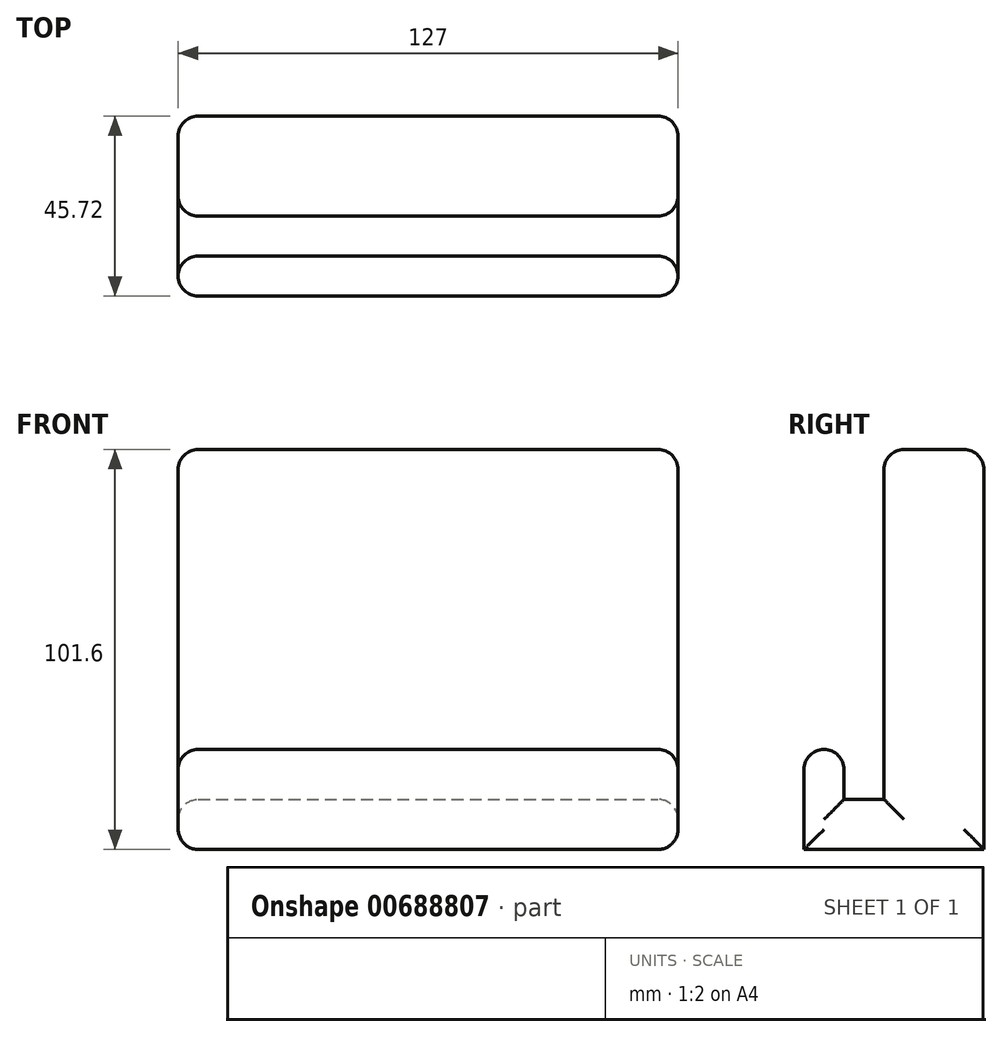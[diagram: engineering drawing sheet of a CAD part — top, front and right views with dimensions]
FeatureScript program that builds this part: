
annotation { "Feature Type Name" : "Feature", "Feature Type Description" : "" }
export const myFeature = defineFeature(function(context is Context, id is Id, definition is map)
    precondition{}
    {
        {
            var Q0;
            Q0=qCreatedBy(makeId("Front.planeOp"),FACE);
            var sketch = newSketch(context, id + "F0", { "sketchPlane" : qUnion([Q0])});
            skLineSegment(sketch, "E0", {"start": v(0, 0) * mm, "end": v(-127, 0) * mm});
            skLineSegment(sketch, "E1", {"start": v(-127, 0) * mm, "end": v(-127, 101.6) * mm});
            skLineSegment(sketch, "E2", {"start": v(0, 0) * mm, "end": v(0, 101.6) * mm});
            skLineSegment(sketch, "E3", {"start": v(0, 101.6) * mm, "end": v(-127, 101.6) * mm});
            skSolve(sketch);
        }
        {
            var Q0;
            Q0=makeQuery(id+"F0.imprint","IMPRINT",FACE,{"disambiguationData":[TD([[makeQuery(id+"F0.imprint","IMPRINT",EDGE,{"derivedFrom":sQuery(id+"F0.wireOp",EDGE,"E0")}),-1.0]])]});
            extrude(context, id + "F1", {"entities" : qUnion([Q0]), "depth" : 25.4 * mm, "offsetDistance" : 25.4 * mm});
        }
        {
            var Q0;
            Q0=makeQuery(id+"F1.opExtrude","CAP_FACE",FACE,{"disambiguationData":[OSD([sQuery(id+"F0.wireOp",EDGE,"E0"),sQuery(id+"F0.wireOp",EDGE,"E1"),sQuery(id+"F0.wireOp",EDGE,"E2"),sQuery(id+"F0.wireOp",EDGE,"E3")])],"isStart":false});
            var sketch = newSketch(context, id + "F2", { "sketchPlane" : qUnion([Q0])});
            skLineSegment(sketch, "E4", {"start": v(-127, 0) * mm, "end": v(-127, 12.7) * mm});
            skLineSegment(sketch, "E5", {"start": v(-127, 12.7) * mm, "end": v(0, 12.7) * mm});
            skLineSegment(sketch, "E6", {"start": v(0, 12.7) * mm, "end": v(0, 0) * mm});
            skLineSegment(sketch, "E7", {"start": v(0, 0) * mm, "end": v(-127, 0) * mm});
            skSolve(sketch);
        }
        {
            var Q0;
            Q0=makeQuery(id+"F2.imprint","IMPRINT",FACE,{"disambiguationData":[TD([[makeQuery(id+"F2.imprint","IMPRINT",EDGE,{"derivedFrom":sQuery(id+"F2.wireOp",EDGE,"E4")}),-1.0]])]});
            extrude(context, id + "F3", {"entities" : qUnion([Q0]), "operationType" : NewBodyOperationType.ADD, "depth" : 20.32 * mm, "offsetDistance" : 25.4 * mm});
        }
        {
            var Q0;
            Q0=makeQuery(id+"F3.opExtrude","SWEPT_FACE",FACE,{"disambiguationData":[OSD([sQuery(id+"F2.wireOp",EDGE,"E5")])]});
            var sketch = newSketch(context, id + "F4", { "sketchPlane" : qUnion([Q0])});
            skLineSegment(sketch, "E8", {"start": v(-127, -45.72) * mm, "end": v(-127, -35.56) * mm});
            skLineSegment(sketch, "E9", {"start": v(-127, -35.56) * mm, "end": v(0, -35.56) * mm});
            skLineSegment(sketch, "E10", {"start": v(0, -35.56) * mm, "end": v(0, -45.72) * mm});
            skLineSegment(sketch, "E11", {"start": v(0, -45.72) * mm, "end": v(-127, -45.72) * mm});
            skSolve(sketch);
        }
        {
            var Q0;
            Q0=makeQuery(id+"F4.imprint","IMPRINT",FACE,{"disambiguationData":[TD([[makeQuery(id+"F4.imprint","IMPRINT",EDGE,{"derivedFrom":sQuery(id+"F4.wireOp",EDGE,"E8")}),-1.0]])]});
            extrude(context, id + "F5", {"entities" : qUnion([Q0]), "operationType" : NewBodyOperationType.ADD, "depth" : 12.7 * mm, "offsetDistance" : 25.4 * mm});
        }
        {
            var Q0;
            Q0=makeQuery(id+"F1.opExtrude","SWEPT_EDGE",EDGE,{"disambiguationData":[OSD([sQuery(id+"F0.wireOp",EDGE,"E2"),sQuery(id+"F0.wireOp",EDGE,"E3")])]});
            fillet(context, id + "F6", {"entities" : qUnion([Q0]), "radius" : 5.08 * mm, "tangentPropagation" : true, "allowEdgeOverflow" : false});
        }
        {
            var Q0;
            Q0=makeQuery(id+"F5.boolean.opBoolean","MERGE",FACE,{"derivedFrom":[makeQuery(id+"F3.boolean.opBoolean","MERGE",FACE,{"derivedFrom":[makeQuery(id+"F1.opExtrude","SWEPT_FACE",FACE,{"disambiguationData":[OSD([sQuery(id+"F0.wireOp",EDGE,"E1")])]}),makeQuery(id+"F3.opExtrude","SWEPT_FACE",FACE,{"disambiguationData":[OSD([sQuery(id+"F2.wireOp",EDGE,"E4")])]})]}),makeQuery(id+"F5.opExtrude","SWEPT_FACE",FACE,{"disambiguationData":[OSD([sQuery(id+"F4.wireOp",EDGE,"E8")])]})]});
            fillet(context, id + "F7", {"entities" : qUnion([Q0]), "radius" : 5.08 * mm, "tangentPropagation" : true, "allowEdgeOverflow" : false});
        }
        {
            var Q0;
            Q0=makeQuery(id+"F5.boolean.opBoolean","MERGE",FACE,{"derivedFrom":[makeQuery(id+"F3.boolean.opBoolean","MERGE",FACE,{"derivedFrom":[makeQuery(id+"F1.opExtrude","SWEPT_FACE",FACE,{"disambiguationData":[OSD([sQuery(id+"F0.wireOp",EDGE,"E2")])]}),makeQuery(id+"F3.opExtrude","SWEPT_FACE",FACE,{"disambiguationData":[OSD([sQuery(id+"F2.wireOp",EDGE,"E6")])]})]}),makeQuery(id+"F5.opExtrude","SWEPT_FACE",FACE,{"disambiguationData":[OSD([sQuery(id+"F4.wireOp",EDGE,"E10")])]})]});
            fillet(context, id + "F8", {"entities" : qUnion([Q0]), "radius" : 5.08 * mm, "tangentPropagation" : true, "allowEdgeOverflow" : false});
        }
        {
            var Q0;
            Q0=makeQuery(id+"F5.opExtrude","CAP_FACE",FACE,{"disambiguationData":[OSD([sQuery(id+"F4.wireOp",EDGE,"E8"),sQuery(id+"F4.wireOp",EDGE,"E9"),sQuery(id+"F4.wireOp",EDGE,"E10"),sQuery(id+"F4.wireOp",EDGE,"E11")])],"isStart":false});
            fillet(context, id + "F9", {"entities" : qUnion([Q0]), "radius" : 5.08 * mm, "tangentPropagation" : true, "allowEdgeOverflow" : false});
        }
    });
